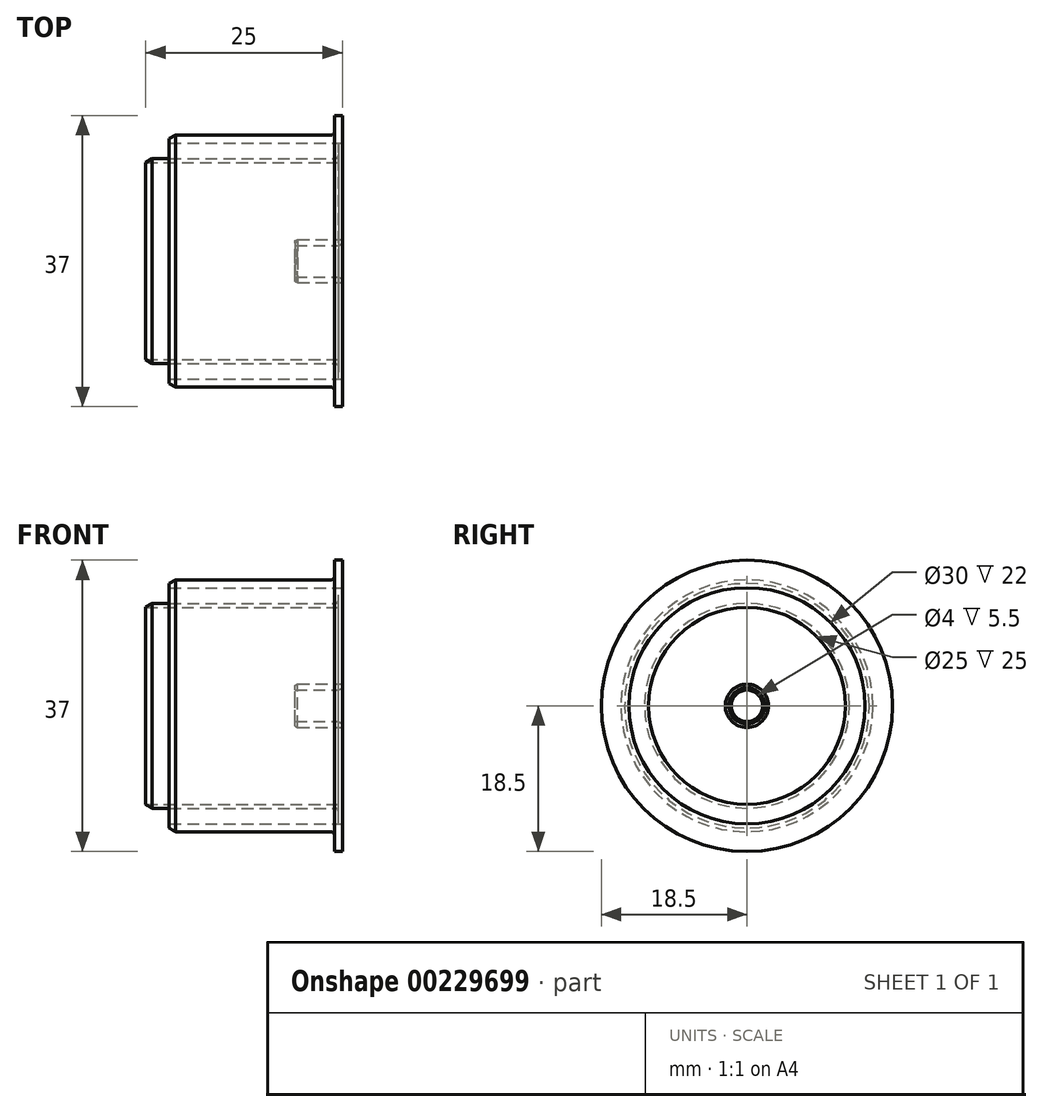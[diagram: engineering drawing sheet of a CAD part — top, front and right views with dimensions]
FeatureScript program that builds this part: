
annotation { "Feature Type Name" : "Feature", "Feature Type Description" : "" }
export const myFeature = defineFeature(function(context is Context, id is Id, definition is map)
    precondition{}
    {
        {
            var Q0;
            Q0=qCreatedBy(makeId("Front.planeOp"),FACE);
            var sketch = newSketch(context, id + "F0", { "sketchPlane" : qUnion([Q0])});
            skLineSegment(sketch, "E0", {"start": v(0, -12.5) * mm, "end": v(-25, -12.5) * mm});
            skLineSegment(sketch, "E1", {"start": v(-25, -12.5) * mm, "end": v(-25, -12.54) * mm});
            skLineSegment(sketch, "E2", {"start": v(-25, -12.54) * mm, "end": v(-24.2, -13) * mm});
            skLineSegment(sketch, "E3", {"start": v(-24.2, -13) * mm, "end": v(-1, -13) * mm});
            skLineSegment(sketch, "E4", {"start": v(-0.5, -13.5) * mm, "end": v(-0.5, -15) * mm});
            skLineSegment(sketch, "E5", {"start": v(-0.5, -15) * mm, "end": v(0, -15) * mm});
            skLineSegment(sketch, "E6", {"start": v(0, -15) * mm, "end": v(0, -12.5) * mm});
            skLineSegment(sketch, "E7", {"start": v(0, 0) * mm, "end": v(-25, 0) * mm, "construction": true});
            skPoint(sketch, "E8.visualSharp", {"position": v(-0.5, -13) * mm});
            skArc(sketch, "E8.filletArc", {"start": v(-0.5, -13.5) * mm, "mid": v(-0.65, -13.15) * mm, "end": v(-1, -13) * mm});
            skSolve(sketch);
        }
        {
            var Q0;
            Q0=makeQuery(id+"F0.imprint","IMPRINT",FACE,{"disambiguationData":[TD([[makeQuery(id+"F0.imprint","IMPRINT",EDGE,{"derivedFrom":sQuery(id+"F0.wireOp",EDGE,"E0")}),1.0]])]});
            var Q1;
            Q1=sQuery(id+"F0.wireOp",EDGE,"E7");
            revolve(context, id + "F1", {"entities" : qUnion([Q0]), "axis" : qUnion([Q1]), "revolveType" : RevolveType.FULL});
        }
        {
            var Q0;
            Q0=qCreatedBy(makeId("Front.planeOp"),FACE);
            var sketch = newSketch(context, id + "F2", { "sketchPlane" : qUnion([Q0])});
            skLineSegment(sketch, "E9", {"start": v(0, -2.29) * mm, "end": v(-0.5, -2) * mm});
            skLineSegment(sketch, "E10", {"start": v(-0.5, -2) * mm, "end": v(-6, -2) * mm});
            skLineSegment(sketch, "E11", {"start": v(-6, -2) * mm, "end": v(-6, -2.58) * mm});
            skLineSegment(sketch, "E12", {"start": v(-6, -2.58) * mm, "end": v(-5.7, -2.75) * mm});
            skLineSegment(sketch, "E13", {"start": v(-5.7, -2.75) * mm, "end": v(0, -2.75) * mm});
            skLineSegment(sketch, "E14", {"start": v(0, -2.75) * mm, "end": v(0, -2.29) * mm});
            skLineSegment(sketch, "E15", {"start": v(0, 0) * mm, "end": v(-6, 0) * mm, "construction": true});
            skSolve(sketch);
        }
        {
            var Q0;
            Q0=makeQuery(id+"F2.imprint","IMPRINT",FACE,{"disambiguationData":[TD([[makeQuery(id+"F2.imprint","IMPRINT",EDGE,{"derivedFrom":sQuery(id+"F2.wireOp",EDGE,"E9")}),1.0]])]});
            var Q1;
            Q1=sQuery(id+"F2.wireOp",EDGE,"E15");
            revolve(context, id + "F3", {"entities" : qUnion([Q0]), "axis" : qUnion([Q1]), "revolveType" : RevolveType.FULL});
        }
        {
            var Q0;
            Q0=qCreatedBy(makeId("Top.planeOp"),FACE);
            var sketch = newSketch(context, id + "F4", { "sketchPlane" : qUnion([Q0])});
            skLineSegment(sketch, "E16", {"start": v(0, -15) * mm, "end": v(-22, -15) * mm});
            skLineSegment(sketch, "E17", {"start": v(-22, -15) * mm, "end": v(-22, -15.54) * mm});
            skLineSegment(sketch, "E18", {"start": v(-22, -15.54) * mm, "end": v(-21.2, -16) * mm});
            skLineSegment(sketch, "E19", {"start": v(-21.2, -16) * mm, "end": v(-1.5, -16) * mm});
            skLineSegment(sketch, "E20", {"start": v(-1, -16.5) * mm, "end": v(-1, -18.5) * mm});
            skLineSegment(sketch, "E21", {"start": v(-1, -18.5) * mm, "end": v(0, -18.5) * mm});
            skLineSegment(sketch, "E22", {"start": v(0, -18.5) * mm, "end": v(0, -15) * mm});
            skPoint(sketch, "E23.visualSharp", {"position": v(-1, -16) * mm});
            skArc(sketch, "E23.filletArc", {"start": v(-1, -16.5) * mm, "mid": v(-1.15, -16.15) * mm, "end": v(-1.5, -16) * mm});
            skLineSegment(sketch, "E24", {"start": v(0, 0) * mm, "end": v(-22, 0) * mm, "construction": true});
            skSolve(sketch);
        }
        {
            var Q0;
            Q0=makeQuery(id+"F4.imprint","IMPRINT",FACE,{"disambiguationData":[TD([[makeQuery(id+"F4.imprint","IMPRINT",EDGE,{"derivedFrom":sQuery(id+"F4.wireOp",EDGE,"E16")}),1.0]])]});
            var Q1;
            Q1=sQuery(id+"F4.wireOp",EDGE,"E24");
            revolve(context, id + "F5", {"entities" : qUnion([Q0]), "axis" : qUnion([Q1]), "revolveType" : RevolveType.FULL});
        }
    });
